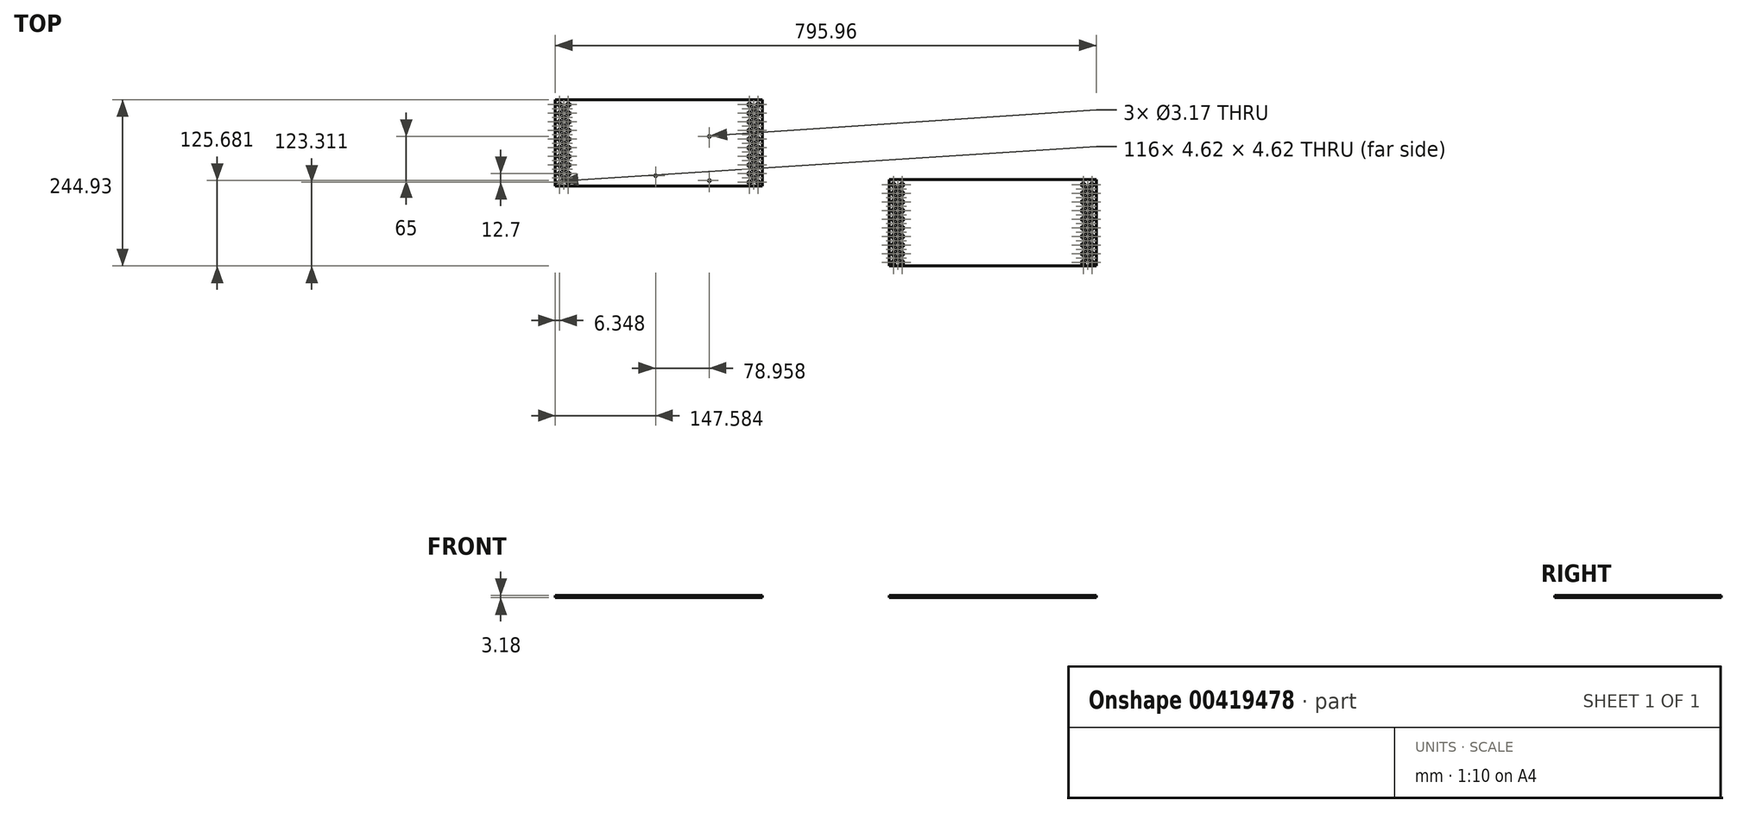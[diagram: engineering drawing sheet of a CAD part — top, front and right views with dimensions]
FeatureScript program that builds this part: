
annotation { "Feature Type Name" : "Feature", "Feature Type Description" : "" }
export const myFeature = defineFeature(function(context is Context, id is Id, definition is map)
    precondition{}
    {
        {
            var Q0;
            Q0=qCreatedBy(makeId("Top.planeOp"),FACE);
            var sketch = newSketch(context, id + "F0", { "sketchPlane" : qUnion([Q0])});
            skLineSegment(sketch, "E0", {"start": v(0, 0) * mm, "end": v(0, 127) * mm});
            skLineSegment(sketch, "E1", {"start": v(0, 127) * mm, "end": v(304.8, 127) * mm});
            skLineSegment(sketch, "E2", {"start": v(304.8, 127) * mm, "end": v(304.8, 0) * mm});
            skLineSegment(sketch, "E3", {"start": v(304.8, 0) * mm, "end": v(0, 0) * mm});
            skLineSegment(sketch, "E4", {"start": v(304.8, 0) * mm, "end": v(304.8, 127) * mm});
            skLineSegment(sketch, "E5", {"start": v(300.76, 3.07) * mm, "end": v(300.76, 7.7) * mm});
            skLineSegment(sketch, "E6.top", {"start": v(296.14, 3.07) * mm, "end": v(296.14, 7.7) * mm});
            skLineSegment(sketch, "E6.left", {"start": v(300.76, 3.07) * mm, "end": v(296.14, 3.07) * mm});
            skLineSegment(sketch, "E6.right", {"start": v(300.76, 7.7) * mm, "end": v(296.14, 7.7) * mm});
            skLineSegment(sketch, "E7", {"start": v(298.45, 7.7) * mm, "end": v(296.14, 7.7) * mm});
            skLineSegment(sketch, "E8", {"start": v(300.76, 5.38) * mm, "end": v(300.76, 7.7) * mm});
            skLineSegment(sketch, "E9.bottom", {"start": v(294.41, 9.42) * mm, "end": v(294.41, 14.05) * mm});
            skLineSegment(sketch, "E9.top", {"start": v(289.79, 9.42) * mm, "end": v(289.79, 14.05) * mm});
            skLineSegment(sketch, "E9.left", {"start": v(294.41, 9.42) * mm, "end": v(289.79, 9.42) * mm});
            skLineSegment(sketch, "E9.right", {"start": v(294.41, 14.05) * mm, "end": v(289.79, 14.05) * mm});
            skLineSegment(sketch, "E10.trimOffspring", {"start": v(300.76, 15.77) * mm, "end": v(300.76, 20.4) * mm});
            skLineSegment(sketch, "E11.1.0.0", {"start": v(289.79, 22.12) * mm, "end": v(289.79, 26.75) * mm});
            skLineSegment(sketch, "E11.1.0.1", {"start": v(294.41, 22.12) * mm, "end": v(294.41, 26.75) * mm});
            skLineSegment(sketch, "E11.1.0.2", {"start": v(294.41, 22.12) * mm, "end": v(289.79, 22.12) * mm});
            skLineSegment(sketch, "E11.1.0.3", {"start": v(294.41, 26.75) * mm, "end": v(289.79, 26.75) * mm});
            skLineSegment(sketch, "E11.1.0.4", {"start": v(300.76, 20.4) * mm, "end": v(296.14, 20.4) * mm});
            skLineSegment(sketch, "E11.1.0.5", {"start": v(296.14, 15.77) * mm, "end": v(296.14, 20.4) * mm});
            skLineSegment(sketch, "E11.1.0.6", {"start": v(300.76, 15.77) * mm, "end": v(296.14, 15.77) * mm});
            skLineSegment(sketch, "E11.2.0.0", {"start": v(289.79, 34.82) * mm, "end": v(289.79, 39.45) * mm});
            skLineSegment(sketch, "E11.2.0.1", {"start": v(294.41, 34.82) * mm, "end": v(294.41, 39.45) * mm});
            skLineSegment(sketch, "E11.2.0.2", {"start": v(294.41, 34.82) * mm, "end": v(289.79, 34.82) * mm});
            skLineSegment(sketch, "E11.2.0.3", {"start": v(294.41, 39.45) * mm, "end": v(289.79, 39.45) * mm});
            skLineSegment(sketch, "E11.2.0.4", {"start": v(300.76, 33.1) * mm, "end": v(296.14, 33.1) * mm});
            skLineSegment(sketch, "E11.2.0.5", {"start": v(296.14, 28.47) * mm, "end": v(296.14, 33.1) * mm});
            skLineSegment(sketch, "E11.2.0.6", {"start": v(300.76, 28.47) * mm, "end": v(296.14, 28.47) * mm});
            skLineSegment(sketch, "E11.2.0.7", {"start": v(300.76, 28.47) * mm, "end": v(300.76, 33.1) * mm});
            skLineSegment(sketch, "E11.3.0.0", {"start": v(289.79, 47.52) * mm, "end": v(289.79, 52.15) * mm});
            skLineSegment(sketch, "E11.3.0.1", {"start": v(294.41, 47.52) * mm, "end": v(294.41, 52.15) * mm});
            skLineSegment(sketch, "E11.3.0.2", {"start": v(294.41, 47.52) * mm, "end": v(289.79, 47.52) * mm});
            skLineSegment(sketch, "E11.3.0.3", {"start": v(294.41, 52.15) * mm, "end": v(289.79, 52.15) * mm});
            skLineSegment(sketch, "E11.3.0.4", {"start": v(300.76, 45.8) * mm, "end": v(296.14, 45.8) * mm});
            skLineSegment(sketch, "E11.3.0.5", {"start": v(296.14, 41.17) * mm, "end": v(296.14, 45.8) * mm});
            skLineSegment(sketch, "E11.3.0.6", {"start": v(300.76, 41.17) * mm, "end": v(296.14, 41.17) * mm});
            skLineSegment(sketch, "E11.3.0.7", {"start": v(300.76, 41.17) * mm, "end": v(300.76, 45.8) * mm});
            skLineSegment(sketch, "E11.4.0.0", {"start": v(289.79, 60.22) * mm, "end": v(289.79, 64.85) * mm});
            skLineSegment(sketch, "E11.4.0.1", {"start": v(294.41, 60.22) * mm, "end": v(294.41, 64.85) * mm});
            skLineSegment(sketch, "E11.4.0.2", {"start": v(294.41, 60.22) * mm, "end": v(289.79, 60.22) * mm});
            skLineSegment(sketch, "E11.4.0.3", {"start": v(294.41, 64.85) * mm, "end": v(289.79, 64.85) * mm});
            skLineSegment(sketch, "E11.4.0.4", {"start": v(300.76, 58.5) * mm, "end": v(296.14, 58.5) * mm});
            skLineSegment(sketch, "E11.4.0.5", {"start": v(296.14, 53.87) * mm, "end": v(296.14, 58.5) * mm});
            skLineSegment(sketch, "E11.4.0.6", {"start": v(300.76, 53.87) * mm, "end": v(296.14, 53.87) * mm});
            skLineSegment(sketch, "E11.4.0.7", {"start": v(300.76, 53.87) * mm, "end": v(300.76, 58.5) * mm});
            skLineSegment(sketch, "E11.5.0.0", {"start": v(289.79, 72.92) * mm, "end": v(289.79, 77.55) * mm});
            skLineSegment(sketch, "E11.5.0.1", {"start": v(294.41, 72.92) * mm, "end": v(294.41, 77.55) * mm});
            skLineSegment(sketch, "E11.5.0.2", {"start": v(294.41, 72.92) * mm, "end": v(289.79, 72.92) * mm});
            skLineSegment(sketch, "E11.5.0.3", {"start": v(294.41, 77.55) * mm, "end": v(289.79, 77.55) * mm});
            skLineSegment(sketch, "E11.5.0.4", {"start": v(300.76, 71.2) * mm, "end": v(296.14, 71.2) * mm});
            skLineSegment(sketch, "E11.5.0.5", {"start": v(296.14, 66.57) * mm, "end": v(296.14, 71.2) * mm});
            skLineSegment(sketch, "E11.5.0.6", {"start": v(300.76, 66.57) * mm, "end": v(296.14, 66.57) * mm});
            skLineSegment(sketch, "E11.5.0.7", {"start": v(300.76, 66.57) * mm, "end": v(300.76, 71.2) * mm});
            skLineSegment(sketch, "E11.6.0.0", {"start": v(289.79, 85.62) * mm, "end": v(289.79, 90.25) * mm});
            skLineSegment(sketch, "E11.6.0.1", {"start": v(294.41, 85.62) * mm, "end": v(294.41, 90.25) * mm});
            skLineSegment(sketch, "E11.6.0.2", {"start": v(294.41, 85.62) * mm, "end": v(289.79, 85.62) * mm});
            skLineSegment(sketch, "E11.6.0.3", {"start": v(294.41, 90.25) * mm, "end": v(289.79, 90.25) * mm});
            skLineSegment(sketch, "E11.6.0.4", {"start": v(300.76, 83.9) * mm, "end": v(296.14, 83.9) * mm});
            skLineSegment(sketch, "E11.6.0.5", {"start": v(296.14, 79.27) * mm, "end": v(296.14, 83.9) * mm});
            skLineSegment(sketch, "E11.6.0.6", {"start": v(300.76, 79.27) * mm, "end": v(296.14, 79.27) * mm});
            skLineSegment(sketch, "E11.6.0.7", {"start": v(300.76, 79.27) * mm, "end": v(300.76, 83.9) * mm});
            skLineSegment(sketch, "E11.7.0.0", {"start": v(289.79, 98.32) * mm, "end": v(289.79, 102.95) * mm});
            skLineSegment(sketch, "E11.7.0.1", {"start": v(294.41, 98.32) * mm, "end": v(294.41, 102.95) * mm});
            skLineSegment(sketch, "E11.7.0.2", {"start": v(294.41, 98.32) * mm, "end": v(289.79, 98.32) * mm});
            skLineSegment(sketch, "E11.7.0.3", {"start": v(294.41, 102.95) * mm, "end": v(289.79, 102.95) * mm});
            skLineSegment(sketch, "E11.7.0.4", {"start": v(300.76, 96.6) * mm, "end": v(296.14, 96.6) * mm});
            skLineSegment(sketch, "E11.7.0.5", {"start": v(296.14, 91.97) * mm, "end": v(296.14, 96.6) * mm});
            skLineSegment(sketch, "E11.7.0.6", {"start": v(300.76, 91.97) * mm, "end": v(296.14, 91.97) * mm});
            skLineSegment(sketch, "E11.7.0.7", {"start": v(300.76, 91.97) * mm, "end": v(300.76, 96.6) * mm});
            skLineSegment(sketch, "E11.8.0.0", {"start": v(289.79, 111.02) * mm, "end": v(289.79, 115.65) * mm});
            skLineSegment(sketch, "E11.8.0.1", {"start": v(294.41, 111.02) * mm, "end": v(294.41, 115.65) * mm});
            skLineSegment(sketch, "E11.8.0.2", {"start": v(294.41, 111.02) * mm, "end": v(289.79, 111.02) * mm});
            skLineSegment(sketch, "E11.8.0.3", {"start": v(294.41, 115.65) * mm, "end": v(289.79, 115.65) * mm});
            skLineSegment(sketch, "E11.8.0.4", {"start": v(300.76, 109.3) * mm, "end": v(296.14, 109.3) * mm});
            skLineSegment(sketch, "E11.8.0.5", {"start": v(296.14, 104.67) * mm, "end": v(296.14, 109.3) * mm});
            skLineSegment(sketch, "E11.8.0.6", {"start": v(300.76, 104.67) * mm, "end": v(296.14, 104.67) * mm});
            skLineSegment(sketch, "E11.8.0.7", {"start": v(300.76, 104.67) * mm, "end": v(300.76, 109.3) * mm});
            skLineSegment(sketch, "E11.9.0.4", {"start": v(300.76, 122) * mm, "end": v(296.14, 122) * mm});
            skLineSegment(sketch, "E11.9.0.5", {"start": v(296.14, 117.37) * mm, "end": v(296.14, 122) * mm});
            skLineSegment(sketch, "E11.9.0.6", {"start": v(300.76, 117.37) * mm, "end": v(296.14, 117.37) * mm});
            skLineSegment(sketch, "E11.9.0.7", {"start": v(300.76, 117.37) * mm, "end": v(300.76, 122) * mm});
            skLineSegment(sketch, "E11.direction1", {"start": v(294.41, 9.42) * mm, "end": v(294.41, 22.12) * mm, "construction": true});
            skLineSegment(sketch, "E12.1.0.20", {"start": v(288.06, 20.4) * mm, "end": v(283.44, 20.4) * mm});
            skLineSegment(sketch, "E12.1.0.21", {"start": v(288.06, 122) * mm, "end": v(283.44, 122) * mm});
            skLineSegment(sketch, "E12.1.0.22", {"start": v(288.06, 96.6) * mm, "end": v(283.44, 96.6) * mm});
            skLineSegment(sketch, "E12.1.0.23", {"start": v(288.06, 71.2) * mm, "end": v(283.44, 71.2) * mm});
            skLineSegment(sketch, "E12.1.0.24", {"start": v(288.06, 45.8) * mm, "end": v(283.44, 45.8) * mm});
            skLineSegment(sketch, "E12.1.0.36", {"start": v(283.44, 15.79) * mm, "end": v(283.44, 20.4) * mm});
            skLineSegment(sketch, "E12.1.0.39", {"start": v(283.44, 117.39) * mm, "end": v(283.44, 122) * mm});
            skLineSegment(sketch, "E12.1.0.41", {"start": v(283.44, 91.99) * mm, "end": v(283.44, 96.6) * mm});
            skLineSegment(sketch, "E12.1.0.42", {"start": v(283.44, 66.59) * mm, "end": v(283.44, 71.2) * mm});
            skLineSegment(sketch, "E12.1.0.43", {"start": v(283.44, 41.19) * mm, "end": v(283.44, 45.8) * mm});
            skLineSegment(sketch, "E12.1.0.49", {"start": v(288.06, 66.59) * mm, "end": v(283.44, 66.59) * mm});
            skLineSegment(sketch, "E12.1.0.50", {"start": v(288.06, 41.19) * mm, "end": v(283.44, 41.19) * mm});
            skLineSegment(sketch, "E12.1.0.51", {"start": v(288.06, 15.79) * mm, "end": v(283.44, 15.79) * mm});
            skLineSegment(sketch, "E12.1.0.54", {"start": v(288.06, 117.39) * mm, "end": v(283.44, 117.39) * mm});
            skLineSegment(sketch, "E12.1.0.55", {"start": v(288.06, 91.99) * mm, "end": v(283.44, 91.99) * mm});
            skLineSegment(sketch, "E12.1.0.59", {"start": v(288.06, 66.59) * mm, "end": v(288.06, 71.2) * mm});
            skLineSegment(sketch, "E12.1.0.96", {"start": v(288.06, 109.3) * mm, "end": v(283.44, 109.3) * mm});
            skLineSegment(sketch, "E12.1.0.97", {"start": v(288.06, 83.9) * mm, "end": v(283.44, 83.9) * mm});
            skLineSegment(sketch, "E12.1.0.98", {"start": v(288.06, 58.5) * mm, "end": v(283.44, 58.5) * mm});
            skLineSegment(sketch, "E12.1.0.99", {"start": v(288.06, 33.1) * mm, "end": v(283.44, 33.1) * mm});
            skLineSegment(sketch, "E12.1.0.116", {"start": v(283.44, 104.69) * mm, "end": v(283.44, 109.3) * mm});
            skLineSegment(sketch, "E12.1.0.117", {"start": v(283.44, 79.29) * mm, "end": v(283.44, 83.9) * mm});
            skLineSegment(sketch, "E12.1.0.118", {"start": v(283.44, 53.89) * mm, "end": v(283.44, 58.5) * mm});
            skLineSegment(sketch, "E12.1.0.119", {"start": v(283.44, 28.49) * mm, "end": v(283.44, 33.1) * mm});
            skLineSegment(sketch, "E12.1.0.125", {"start": v(288.06, 104.69) * mm, "end": v(283.44, 104.69) * mm});
            skLineSegment(sketch, "E12.1.0.126", {"start": v(288.06, 79.29) * mm, "end": v(283.44, 79.29) * mm});
            skLineSegment(sketch, "E12.1.0.127", {"start": v(288.06, 53.89) * mm, "end": v(283.44, 53.89) * mm});
            skLineSegment(sketch, "E12.1.0.128", {"start": v(288.06, 28.49) * mm, "end": v(283.44, 28.49) * mm});
            skLineSegment(sketch, "E12.1.0.137", {"start": v(283.44, 3.09) * mm, "end": v(283.44, 7.7) * mm});
            skLineSegment(sketch, "E12.1.0.138", {"start": v(288.06, 3.09) * mm, "end": v(283.44, 3.09) * mm});
            skLineSegment(sketch, "E12.1.0.154", {"start": v(288.06, 53.89) * mm, "end": v(288.06, 58.5) * mm});
            skLineSegment(sketch, "E12.1.0.155", {"start": v(288.06, 117.39) * mm, "end": v(288.06, 122) * mm});
            skLineSegment(sketch, "E12.1.0.156", {"start": v(288.06, 41.19) * mm, "end": v(288.06, 45.8) * mm});
            skLineSegment(sketch, "E12.1.0.157", {"start": v(285.75, 7.7) * mm, "end": v(283.44, 7.7) * mm});
            skLineSegment(sketch, "E12.1.0.159", {"start": v(288.06, 91.99) * mm, "end": v(288.06, 96.6) * mm});
            skLineSegment(sketch, "E12.1.0.160", {"start": v(288.06, 104.69) * mm, "end": v(288.06, 109.3) * mm});
            skLineSegment(sketch, "E12.1.0.161", {"start": v(288.06, 28.49) * mm, "end": v(288.06, 33.1) * mm});
            skLineSegment(sketch, "E12.1.0.162", {"start": v(288.06, 79.29) * mm, "end": v(288.06, 83.9) * mm});
            skLineSegment(sketch, "E12.1.0.163", {"start": v(288.06, 15.79) * mm, "end": v(288.06, 20.4) * mm});
            skLineSegment(sketch, "E12.1.0.164", {"start": v(288.06, 28.49) * mm, "end": v(288.06, 33.1) * mm});
            skLineSegment(sketch, "E12.1.0.166", {"start": v(288.06, 41.19) * mm, "end": v(288.06, 45.8) * mm});
            skLineSegment(sketch, "E12.1.0.167", {"start": v(288.06, 15.79) * mm, "end": v(288.06, 20.4) * mm});
            skLineSegment(sketch, "E12.1.0.168", {"start": v(288.06, 117.39) * mm, "end": v(288.06, 122) * mm});
            skLineSegment(sketch, "E12.1.0.169", {"start": v(288.06, 91.99) * mm, "end": v(288.06, 96.6) * mm});
            skLineSegment(sketch, "E12.1.0.170", {"start": v(288.06, 79.29) * mm, "end": v(288.06, 83.9) * mm});
            skLineSegment(sketch, "E12.1.0.171", {"start": v(288.06, 3.09) * mm, "end": v(288.06, 7.7) * mm});
            skLineSegment(sketch, "E12.1.0.172", {"start": v(288.06, 7.7) * mm, "end": v(283.44, 7.7) * mm});
            skLineSegment(sketch, "E12.1.0.173", {"start": v(288.06, 5.4) * mm, "end": v(288.06, 7.7) * mm});
            skLineSegment(sketch, "E12.1.0.174", {"start": v(288.06, 104.69) * mm, "end": v(288.06, 109.3) * mm});
            skLineSegment(sketch, "E12.1.0.175", {"start": v(288.06, 3.09) * mm, "end": v(288.06, 7.7) * mm});
            skLineSegment(sketch, "E13", {"start": v(279.4, 0) * mm, "end": v(304.8, 0) * mm});
            skLineSegment(sketch, "E14.MirrorCS", {"start": v(16.74, 3.09) * mm, "end": v(16.74, 7.7) * mm});
            skLineSegment(sketch, "E15.MirrorCS", {"start": v(4.04, 3.07) * mm, "end": v(4.04, 7.7) * mm});
            skLineSegment(sketch, "E16.MirrorCS", {"start": v(19.05, 7.7) * mm, "end": v(21.36, 7.7) * mm});
            skLineSegment(sketch, "E17.MirrorCS", {"start": v(16.74, 3.09) * mm, "end": v(21.36, 3.09) * mm});
            skLineSegment(sketch, "E18.MirrorCS", {"start": v(16.74, 7.7) * mm, "end": v(21.36, 7.7) * mm});
            skLineSegment(sketch, "E19.MirrorCS", {"start": v(16.74, 5.4) * mm, "end": v(16.74, 7.7) * mm});
            skLineSegment(sketch, "E20.MirrorCS", {"start": v(4.04, 7.7) * mm, "end": v(8.66, 7.7) * mm});
            skLineSegment(sketch, "E21.MirrorCS", {"start": v(8.66, 3.07) * mm, "end": v(8.66, 7.7) * mm});
            skLineSegment(sketch, "E22.MirrorCS", {"start": v(4.04, 3.07) * mm, "end": v(8.66, 3.07) * mm});
            skLineSegment(sketch, "E23.MirrorCS", {"start": v(6.35, 7.7) * mm, "end": v(8.66, 7.7) * mm});
            skLineSegment(sketch, "E24.MirrorCS", {"start": v(4.04, 5.38) * mm, "end": v(4.04, 7.7) * mm});
            skLineSegment(sketch, "E25.MirrorCS", {"start": v(16.74, 79.29) * mm, "end": v(16.74, 83.9) * mm});
            skLineSegment(sketch, "E26.MirrorCS", {"start": v(16.74, 15.79) * mm, "end": v(16.74, 20.4) * mm});
            skLineSegment(sketch, "E27.MirrorCS", {"start": v(16.74, 91.99) * mm, "end": v(16.74, 96.6) * mm});
            skLineSegment(sketch, "E28.MirrorCS", {"start": v(16.74, 41.19) * mm, "end": v(16.74, 45.8) * mm});
            skLineSegment(sketch, "E29.MirrorCS", {"start": v(16.74, 104.69) * mm, "end": v(16.74, 109.3) * mm});
            skLineSegment(sketch, "E30.MirrorCS", {"start": v(15.01, 9.42) * mm, "end": v(15.01, 14.05) * mm});
            skLineSegment(sketch, "E31.MirrorCS", {"start": v(10.39, 9.42) * mm, "end": v(15.01, 9.42) * mm});
            skLineSegment(sketch, "E32.MirrorCS", {"start": v(16.74, 28.49) * mm, "end": v(16.74, 33.1) * mm});
            skLineSegment(sketch, "E33.MirrorCS", {"start": v(15.01, 22.12) * mm, "end": v(15.01, 26.75) * mm});
            skLineSegment(sketch, "E34.MirrorCS", {"start": v(15.01, 72.92) * mm, "end": v(15.01, 77.55) * mm});
            skLineSegment(sketch, "E35.MirrorCS", {"start": v(15.01, 98.32) * mm, "end": v(15.01, 102.95) * mm});
            skLineSegment(sketch, "E36.MirrorCS", {"start": v(15.01, 47.52) * mm, "end": v(15.01, 52.15) * mm});
            skLineSegment(sketch, "E37.MirrorCS", {"start": v(4.04, 109.3) * mm, "end": v(8.66, 109.3) * mm});
            skLineSegment(sketch, "E38.MirrorCS", {"start": v(4.04, 83.9) * mm, "end": v(8.66, 83.9) * mm});
            skLineSegment(sketch, "E39.MirrorCS", {"start": v(4.04, 33.1) * mm, "end": v(8.66, 33.1) * mm});
            skLineSegment(sketch, "E40.MirrorCS", {"start": v(16.74, 83.9) * mm, "end": v(21.36, 83.9) * mm});
            skLineSegment(sketch, "E41.MirrorCS", {"start": v(10.39, 22.12) * mm, "end": v(10.39, 26.75) * mm});
            skLineSegment(sketch, "E42.MirrorCS", {"start": v(10.39, 98.32) * mm, "end": v(10.39, 102.95) * mm});
            skLineSegment(sketch, "E43.MirrorCS", {"start": v(10.39, 72.92) * mm, "end": v(10.39, 77.55) * mm});
            skLineSegment(sketch, "E44.MirrorCS", {"start": v(10.39, 47.52) * mm, "end": v(10.39, 52.15) * mm});
            skLineSegment(sketch, "E45.MirrorCS", {"start": v(10.39, 22.12) * mm, "end": v(15.01, 22.12) * mm});
            skLineSegment(sketch, "E46.MirrorCS", {"start": v(10.39, 98.32) * mm, "end": v(15.01, 98.32) * mm});
            skLineSegment(sketch, "E47.MirrorCS", {"start": v(10.39, 72.92) * mm, "end": v(15.01, 72.92) * mm});
            skLineSegment(sketch, "E48.MirrorCS", {"start": v(10.39, 47.52) * mm, "end": v(15.01, 47.52) * mm});
            skLineSegment(sketch, "E49.MirrorCS", {"start": v(8.66, 79.27) * mm, "end": v(8.66, 83.9) * mm});
            skLineSegment(sketch, "E50.MirrorCS", {"start": v(8.66, 28.47) * mm, "end": v(8.66, 33.1) * mm});
            skLineSegment(sketch, "E51.MirrorCS", {"start": v(8.66, 104.67) * mm, "end": v(8.66, 109.3) * mm});
            skLineSegment(sketch, "E52.MirrorCS", {"start": v(8.66, 53.87) * mm, "end": v(8.66, 58.5) * mm});
            skLineSegment(sketch, "E53.MirrorCS", {"start": v(10.39, 26.75) * mm, "end": v(15.01, 26.75) * mm});
            skLineSegment(sketch, "E54.MirrorCS", {"start": v(4.04, 117.37) * mm, "end": v(4.04, 122) * mm});
            skLineSegment(sketch, "E55.MirrorCS", {"start": v(10.39, 102.95) * mm, "end": v(15.01, 102.95) * mm});
            skLineSegment(sketch, "E56.MirrorCS", {"start": v(10.39, 77.55) * mm, "end": v(15.01, 77.55) * mm});
            skLineSegment(sketch, "E57.MirrorCS", {"start": v(16.74, 104.69) * mm, "end": v(21.36, 104.69) * mm});
            skLineSegment(sketch, "E58.MirrorCS", {"start": v(4.04, 20.4) * mm, "end": v(8.66, 20.4) * mm});
            skLineSegment(sketch, "E59.MirrorCS", {"start": v(10.39, 9.42) * mm, "end": v(10.39, 22.12) * mm, "construction": true});
            skLineSegment(sketch, "E60.MirrorCS", {"start": v(4.04, 96.6) * mm, "end": v(8.66, 96.6) * mm});
            skLineSegment(sketch, "E61.MirrorCS", {"start": v(4.04, 45.8) * mm, "end": v(8.66, 45.8) * mm});
            skLineSegment(sketch, "E62.MirrorCS", {"start": v(16.74, 79.29) * mm, "end": v(21.36, 79.29) * mm});
            skLineSegment(sketch, "E63.MirrorCS", {"start": v(8.66, 15.77) * mm, "end": v(8.66, 20.4) * mm});
            skLineSegment(sketch, "E64.MirrorCS", {"start": v(4.04, 41.17) * mm, "end": v(4.04, 45.8) * mm});
            skLineSegment(sketch, "E65.MirrorCS", {"start": v(8.66, 41.17) * mm, "end": v(8.66, 45.8) * mm});
            skLineSegment(sketch, "E66.MirrorCS", {"start": v(16.74, 117.39) * mm, "end": v(16.74, 122) * mm});
            skLineSegment(sketch, "E67.MirrorCS", {"start": v(16.74, 33.1) * mm, "end": v(21.36, 33.1) * mm});
            skLineSegment(sketch, "E68.MirrorCS", {"start": v(4.04, 28.47) * mm, "end": v(8.66, 28.47) * mm});
            skLineSegment(sketch, "E69.MirrorCS", {"start": v(4.04, 41.17) * mm, "end": v(8.66, 41.17) * mm});
            skLineSegment(sketch, "E70.MirrorCS", {"start": v(4.04, 15.77) * mm, "end": v(8.66, 15.77) * mm});
            skLineSegment(sketch, "E71.MirrorCS", {"start": v(16.74, 28.49) * mm, "end": v(21.36, 28.49) * mm});
            skLineSegment(sketch, "E72.MirrorCS", {"start": v(16.74, 41.19) * mm, "end": v(21.36, 41.19) * mm});
            skLineSegment(sketch, "E73.MirrorCS", {"start": v(21.36, 3.09) * mm, "end": v(21.36, 7.7) * mm});
            skLineSegment(sketch, "E74.MirrorCS", {"start": v(4.04, 91.97) * mm, "end": v(4.04, 96.6) * mm});
            skLineSegment(sketch, "E75.MirrorCS", {"start": v(15.01, 85.62) * mm, "end": v(15.01, 90.25) * mm});
            skLineSegment(sketch, "E76.MirrorCS", {"start": v(15.01, 60.22) * mm, "end": v(15.01, 64.85) * mm});
            skLineSegment(sketch, "E77.MirrorCS", {"start": v(15.01, 34.82) * mm, "end": v(15.01, 39.45) * mm});
            skLineSegment(sketch, "E78.MirrorCS", {"start": v(15.01, 111.02) * mm, "end": v(15.01, 115.65) * mm});
            skLineSegment(sketch, "E79.MirrorCS", {"start": v(10.39, 85.62) * mm, "end": v(10.39, 90.25) * mm});
            skLineSegment(sketch, "E80.MirrorCS", {"start": v(10.39, 60.22) * mm, "end": v(10.39, 64.85) * mm});
            skLineSegment(sketch, "E81.MirrorCS", {"start": v(10.39, 34.82) * mm, "end": v(10.39, 39.45) * mm});
            skLineSegment(sketch, "E82.MirrorCS", {"start": v(16.74, 91.99) * mm, "end": v(21.36, 91.99) * mm});
            skLineSegment(sketch, "E83.MirrorCS", {"start": v(10.39, 111.02) * mm, "end": v(10.39, 115.65) * mm});
            skLineSegment(sketch, "E84.MirrorCS", {"start": v(10.39, 85.62) * mm, "end": v(15.01, 85.62) * mm});
            skLineSegment(sketch, "E85.MirrorCS", {"start": v(10.39, 60.22) * mm, "end": v(15.01, 60.22) * mm});
            skLineSegment(sketch, "E86.MirrorCS", {"start": v(10.39, 111.02) * mm, "end": v(15.01, 111.02) * mm});
            skLineSegment(sketch, "E87.MirrorCS", {"start": v(10.39, 90.25) * mm, "end": v(15.01, 90.25) * mm});
            skLineSegment(sketch, "E88.MirrorCS", {"start": v(10.39, 115.65) * mm, "end": v(15.01, 115.65) * mm});
            skLineSegment(sketch, "E89.MirrorCS", {"start": v(10.39, 14.05) * mm, "end": v(15.01, 14.05) * mm});
            skLineSegment(sketch, "E90.MirrorCS", {"start": v(10.39, 9.42) * mm, "end": v(10.39, 14.05) * mm});
            skLineSegment(sketch, "E91.MirrorCS", {"start": v(16.74, 45.8) * mm, "end": v(21.36, 45.8) * mm});
            skLineSegment(sketch, "E92.MirrorCS", {"start": v(4.04, 15.77) * mm, "end": v(4.04, 20.4) * mm});
            skLineSegment(sketch, "E93.MirrorCS", {"start": v(4.04, 28.47) * mm, "end": v(4.04, 33.1) * mm});
            skLineSegment(sketch, "E94.MirrorCS", {"start": v(4.04, 79.27) * mm, "end": v(4.04, 83.9) * mm});
            skLineSegment(sketch, "E95.MirrorCS", {"start": v(4.04, 104.67) * mm, "end": v(4.04, 109.3) * mm});
            skLineSegment(sketch, "E96.MirrorCS", {"start": v(4.04, 122) * mm, "end": v(8.66, 122) * mm});
            skLineSegment(sketch, "E97.MirrorCS", {"start": v(4.04, 58.5) * mm, "end": v(8.66, 58.5) * mm});
            skLineSegment(sketch, "E98.MirrorCS", {"start": v(16.74, 122) * mm, "end": v(21.36, 122) * mm});
            skLineSegment(sketch, "E99.MirrorCS", {"start": v(4.04, 117.37) * mm, "end": v(8.66, 117.37) * mm});
            skLineSegment(sketch, "E100.MirrorCS", {"start": v(16.74, 96.6) * mm, "end": v(21.36, 96.6) * mm});
            skLineSegment(sketch, "E101.MirrorCS", {"start": v(16.74, 58.5) * mm, "end": v(21.36, 58.5) * mm});
            skLineSegment(sketch, "E102.MirrorCS", {"start": v(10.39, 52.15) * mm, "end": v(15.01, 52.15) * mm});
            skLineSegment(sketch, "E103.MirrorCS", {"start": v(4.04, 71.2) * mm, "end": v(8.66, 71.2) * mm});
            skLineSegment(sketch, "E104.MirrorCS", {"start": v(4.04, 104.67) * mm, "end": v(8.66, 104.67) * mm});
            skLineSegment(sketch, "E105.MirrorCS", {"start": v(8.66, 66.57) * mm, "end": v(8.66, 71.2) * mm});
            skLineSegment(sketch, "E106.MirrorCS", {"start": v(4.04, 53.87) * mm, "end": v(8.66, 53.87) * mm});
            skLineSegment(sketch, "E107.MirrorCS", {"start": v(4.04, 79.27) * mm, "end": v(8.66, 79.27) * mm});
            skLineSegment(sketch, "E108.MirrorCS", {"start": v(16.74, 71.2) * mm, "end": v(21.36, 71.2) * mm});
            skLineSegment(sketch, "E109.MirrorCS", {"start": v(16.74, 15.79) * mm, "end": v(21.36, 15.79) * mm});
            skLineSegment(sketch, "E110.MirrorCS", {"start": v(16.74, 117.39) * mm, "end": v(21.36, 117.39) * mm});
            skLineSegment(sketch, "E111.MirrorCS", {"start": v(16.74, 53.89) * mm, "end": v(16.74, 58.5) * mm});
            skLineSegment(sketch, "E112.MirrorCS", {"start": v(10.39, 34.82) * mm, "end": v(15.01, 34.82) * mm});
            skLineSegment(sketch, "E113.MirrorCS", {"start": v(16.74, 66.59) * mm, "end": v(16.74, 71.2) * mm});
            skLineSegment(sketch, "E114.MirrorCS", {"start": v(10.39, 64.85) * mm, "end": v(15.01, 64.85) * mm});
            skLineSegment(sketch, "E115.MirrorCS", {"start": v(10.39, 39.45) * mm, "end": v(15.01, 39.45) * mm});
            skLineSegment(sketch, "E116.MirrorCS", {"start": v(16.74, 109.3) * mm, "end": v(21.36, 109.3) * mm});
            skLineSegment(sketch, "E117.MirrorCS", {"start": v(16.74, 20.4) * mm, "end": v(21.36, 20.4) * mm});
            skLineSegment(sketch, "E118.MirrorCS", {"start": v(21.36, 79.29) * mm, "end": v(21.36, 83.9) * mm});
            skLineSegment(sketch, "E119.MirrorCS", {"start": v(21.36, 15.79) * mm, "end": v(21.36, 20.4) * mm});
            skLineSegment(sketch, "E120.MirrorCS", {"start": v(8.66, 117.37) * mm, "end": v(8.66, 122) * mm});
            skLineSegment(sketch, "E121.MirrorCS", {"start": v(21.36, 28.49) * mm, "end": v(21.36, 33.1) * mm});
            skLineSegment(sketch, "E122.MirrorCS", {"start": v(21.36, 91.99) * mm, "end": v(21.36, 96.6) * mm});
            skLineSegment(sketch, "E123.MirrorCS", {"start": v(21.36, 66.59) * mm, "end": v(21.36, 71.2) * mm});
            skLineSegment(sketch, "E124.MirrorCS", {"start": v(21.36, 41.19) * mm, "end": v(21.36, 45.8) * mm});
            skLineSegment(sketch, "E125.MirrorCS", {"start": v(16.74, 53.89) * mm, "end": v(21.36, 53.89) * mm});
            skLineSegment(sketch, "E126.MirrorCS", {"start": v(16.74, 66.59) * mm, "end": v(21.36, 66.59) * mm});
            skLineSegment(sketch, "E127.MirrorCS", {"start": v(4.04, 66.57) * mm, "end": v(8.66, 66.57) * mm});
            skLineSegment(sketch, "E128.MirrorCS", {"start": v(4.04, 66.57) * mm, "end": v(4.04, 71.2) * mm});
            skLineSegment(sketch, "E129.MirrorCS", {"start": v(21.36, 104.69) * mm, "end": v(21.36, 109.3) * mm});
            skLineSegment(sketch, "E130.MirrorCS", {"start": v(4.04, 53.87) * mm, "end": v(4.04, 58.5) * mm});
            skLineSegment(sketch, "E131.MirrorCS", {"start": v(21.36, 117.39) * mm, "end": v(21.36, 122) * mm});
            skLineSegment(sketch, "E132.MirrorCS", {"start": v(21.36, 53.89) * mm, "end": v(21.36, 58.5) * mm});
            skLineSegment(sketch, "E133", {"start": v(8.66, 96.6) * mm, "end": v(8.66, 91.99) * mm});
            skLineSegment(sketch, "E134", {"start": v(8.66, 91.99) * mm, "end": v(4.04, 91.97) * mm});
            skSolve(sketch);
        }
        {
            var Q0;
            Q0=makeQuery(id+"F0.imprint","IMPRINT",FACE,{"disambiguationData":[TD([[makeQuery(id+"F0.imprint","IMPRINT",EDGE,{"derivedFrom":sQuery(id+"F0.wireOp",EDGE,"E0")}),-1.0]])]});
            extrude(context, id + "F1", {"entities" : qUnion([Q0]), "depth" : 3.17 * mm});
        }
        {
            var Q0;
            Q0=qCreatedBy(makeId("Top.planeOp"),FACE);
            var sketch = newSketch(context, id + "F2", { "sketchPlane" : qUnion([Q0])});
            skLineSegment(sketch, "E135", {"start": v(-491.16, 117.93) * mm, "end": v(-491.16, 244.93) * mm});
            skLineSegment(sketch, "E136", {"start": v(-491.16, 244.93) * mm, "end": v(-186.36, 244.93) * mm});
            skLineSegment(sketch, "E137", {"start": v(-186.36, 244.93) * mm, "end": v(-186.36, 117.93) * mm});
            skLineSegment(sketch, "E138", {"start": v(-186.36, 117.93) * mm, "end": v(-491.16, 117.93) * mm});
            skLineSegment(sketch, "E139", {"start": v(-186.36, 117.93) * mm, "end": v(-186.36, 244.93) * mm});
            skLineSegment(sketch, "E140", {"start": v(-190.4, 121) * mm, "end": v(-190.4, 125.62) * mm});
            skLineSegment(sketch, "E141.top", {"start": v(-195.02, 121) * mm, "end": v(-195.02, 125.62) * mm});
            skLineSegment(sketch, "E141.left", {"start": v(-190.4, 121) * mm, "end": v(-195.02, 121) * mm});
            skLineSegment(sketch, "E141.right", {"start": v(-190.4, 125.62) * mm, "end": v(-195.02, 125.62) * mm});
            skLineSegment(sketch, "E142", {"start": v(-192.71, 125.62) * mm, "end": v(-195.02, 125.62) * mm});
            skLineSegment(sketch, "E143", {"start": v(-190.4, 123.31) * mm, "end": v(-190.4, 125.62) * mm});
            skLineSegment(sketch, "E144.bottom", {"start": v(-196.75, 127.35) * mm, "end": v(-196.75, 131.97) * mm});
            skLineSegment(sketch, "E144.top", {"start": v(-201.37, 127.35) * mm, "end": v(-201.37, 131.97) * mm});
            skLineSegment(sketch, "E144.left", {"start": v(-196.75, 127.35) * mm, "end": v(-201.37, 127.35) * mm});
            skLineSegment(sketch, "E144.right", {"start": v(-196.75, 131.97) * mm, "end": v(-201.37, 131.97) * mm});
            skLineSegment(sketch, "E145.trimOffspring", {"start": v(-190.4, 133.7) * mm, "end": v(-190.4, 138.32) * mm});
            skLineSegment(sketch, "E146.1.0.0", {"start": v(-201.37, 140.05) * mm, "end": v(-201.37, 144.67) * mm});
            skLineSegment(sketch, "E146.1.0.1", {"start": v(-196.75, 140.05) * mm, "end": v(-196.75, 144.67) * mm});
            skLineSegment(sketch, "E146.1.0.2", {"start": v(-196.75, 140.05) * mm, "end": v(-201.37, 140.05) * mm});
            skLineSegment(sketch, "E146.1.0.3", {"start": v(-196.75, 144.67) * mm, "end": v(-201.37, 144.67) * mm});
            skLineSegment(sketch, "E146.1.0.4", {"start": v(-190.4, 138.32) * mm, "end": v(-195.02, 138.32) * mm});
            skLineSegment(sketch, "E146.1.0.5", {"start": v(-195.02, 133.7) * mm, "end": v(-195.02, 138.32) * mm});
            skLineSegment(sketch, "E146.1.0.6", {"start": v(-190.4, 133.7) * mm, "end": v(-195.02, 133.7) * mm});
            skLineSegment(sketch, "E146.2.0.0", {"start": v(-201.37, 152.75) * mm, "end": v(-201.37, 157.37) * mm});
            skLineSegment(sketch, "E146.2.0.1", {"start": v(-196.75, 152.75) * mm, "end": v(-196.75, 157.37) * mm});
            skLineSegment(sketch, "E146.2.0.2", {"start": v(-196.75, 152.75) * mm, "end": v(-201.37, 152.75) * mm});
            skLineSegment(sketch, "E146.2.0.3", {"start": v(-196.75, 157.37) * mm, "end": v(-201.37, 157.37) * mm});
            skLineSegment(sketch, "E146.2.0.4", {"start": v(-190.4, 151.02) * mm, "end": v(-195.02, 151.02) * mm});
            skLineSegment(sketch, "E146.2.0.5", {"start": v(-195.02, 146.4) * mm, "end": v(-195.02, 151.02) * mm});
            skLineSegment(sketch, "E146.2.0.6", {"start": v(-190.4, 146.4) * mm, "end": v(-195.02, 146.4) * mm});
            skLineSegment(sketch, "E146.2.0.7", {"start": v(-190.4, 146.4) * mm, "end": v(-190.4, 151.02) * mm});
            skLineSegment(sketch, "E146.3.0.0", {"start": v(-201.37, 165.45) * mm, "end": v(-201.37, 170.07) * mm});
            skLineSegment(sketch, "E146.3.0.1", {"start": v(-196.75, 165.45) * mm, "end": v(-196.75, 170.07) * mm});
            skLineSegment(sketch, "E146.3.0.2", {"start": v(-196.75, 165.45) * mm, "end": v(-201.37, 165.45) * mm});
            skLineSegment(sketch, "E146.3.0.3", {"start": v(-196.75, 170.07) * mm, "end": v(-201.37, 170.07) * mm});
            skLineSegment(sketch, "E146.3.0.4", {"start": v(-190.4, 163.72) * mm, "end": v(-195.02, 163.72) * mm});
            skLineSegment(sketch, "E146.3.0.5", {"start": v(-195.02, 159.1) * mm, "end": v(-195.02, 163.72) * mm});
            skLineSegment(sketch, "E146.3.0.6", {"start": v(-190.4, 159.1) * mm, "end": v(-195.02, 159.1) * mm});
            skLineSegment(sketch, "E146.3.0.7", {"start": v(-190.4, 159.1) * mm, "end": v(-190.4, 163.72) * mm});
            skLineSegment(sketch, "E146.4.0.0", {"start": v(-201.37, 178.15) * mm, "end": v(-201.37, 182.77) * mm});
            skLineSegment(sketch, "E146.4.0.1", {"start": v(-196.75, 178.15) * mm, "end": v(-196.75, 182.77) * mm});
            skLineSegment(sketch, "E146.4.0.2", {"start": v(-196.75, 178.15) * mm, "end": v(-201.37, 178.15) * mm});
            skLineSegment(sketch, "E146.4.0.3", {"start": v(-196.75, 182.77) * mm, "end": v(-201.37, 182.77) * mm});
            skLineSegment(sketch, "E146.4.0.4", {"start": v(-190.4, 176.42) * mm, "end": v(-195.02, 176.42) * mm});
            skLineSegment(sketch, "E146.4.0.5", {"start": v(-195.02, 171.8) * mm, "end": v(-195.02, 176.42) * mm});
            skLineSegment(sketch, "E146.4.0.6", {"start": v(-190.4, 171.8) * mm, "end": v(-195.02, 171.8) * mm});
            skLineSegment(sketch, "E146.4.0.7", {"start": v(-190.4, 171.8) * mm, "end": v(-190.4, 176.42) * mm});
            skLineSegment(sketch, "E146.5.0.0", {"start": v(-201.37, 190.85) * mm, "end": v(-201.37, 195.47) * mm});
            skLineSegment(sketch, "E146.5.0.1", {"start": v(-196.75, 190.85) * mm, "end": v(-196.75, 195.47) * mm});
            skLineSegment(sketch, "E146.5.0.2", {"start": v(-196.75, 190.85) * mm, "end": v(-201.37, 190.85) * mm});
            skLineSegment(sketch, "E146.5.0.3", {"start": v(-196.75, 195.47) * mm, "end": v(-201.37, 195.47) * mm});
            skLineSegment(sketch, "E146.5.0.4", {"start": v(-190.4, 189.12) * mm, "end": v(-195.02, 189.12) * mm});
            skLineSegment(sketch, "E146.5.0.5", {"start": v(-195.02, 184.5) * mm, "end": v(-195.02, 189.12) * mm});
            skLineSegment(sketch, "E146.5.0.6", {"start": v(-190.4, 184.5) * mm, "end": v(-195.02, 184.5) * mm});
            skLineSegment(sketch, "E146.5.0.7", {"start": v(-190.4, 184.5) * mm, "end": v(-190.4, 189.12) * mm});
            skLineSegment(sketch, "E146.6.0.0", {"start": v(-201.37, 203.55) * mm, "end": v(-201.37, 208.17) * mm});
            skLineSegment(sketch, "E146.6.0.1", {"start": v(-196.75, 203.55) * mm, "end": v(-196.75, 208.17) * mm});
            skLineSegment(sketch, "E146.6.0.2", {"start": v(-196.75, 203.55) * mm, "end": v(-201.37, 203.55) * mm});
            skLineSegment(sketch, "E146.6.0.3", {"start": v(-196.75, 208.17) * mm, "end": v(-201.37, 208.17) * mm});
            skLineSegment(sketch, "E146.6.0.4", {"start": v(-190.4, 201.82) * mm, "end": v(-195.02, 201.82) * mm});
            skLineSegment(sketch, "E146.6.0.5", {"start": v(-195.02, 197.2) * mm, "end": v(-195.02, 201.82) * mm});
            skLineSegment(sketch, "E146.6.0.6", {"start": v(-190.4, 197.2) * mm, "end": v(-195.02, 197.2) * mm});
            skLineSegment(sketch, "E146.6.0.7", {"start": v(-190.4, 197.2) * mm, "end": v(-190.4, 201.82) * mm});
            skLineSegment(sketch, "E146.7.0.0", {"start": v(-201.37, 216.25) * mm, "end": v(-201.37, 220.87) * mm});
            skLineSegment(sketch, "E146.7.0.1", {"start": v(-196.75, 216.25) * mm, "end": v(-196.75, 220.87) * mm});
            skLineSegment(sketch, "E146.7.0.2", {"start": v(-196.75, 216.25) * mm, "end": v(-201.37, 216.25) * mm});
            skLineSegment(sketch, "E146.7.0.3", {"start": v(-196.75, 220.87) * mm, "end": v(-201.37, 220.87) * mm});
            skLineSegment(sketch, "E146.7.0.4", {"start": v(-190.4, 214.52) * mm, "end": v(-195.02, 214.52) * mm});
            skLineSegment(sketch, "E146.7.0.5", {"start": v(-195.02, 209.9) * mm, "end": v(-195.02, 214.52) * mm});
            skLineSegment(sketch, "E146.7.0.6", {"start": v(-190.4, 209.9) * mm, "end": v(-195.02, 209.9) * mm});
            skLineSegment(sketch, "E146.7.0.7", {"start": v(-190.4, 209.9) * mm, "end": v(-190.4, 214.52) * mm});
            skLineSegment(sketch, "E146.8.0.0", {"start": v(-201.37, 228.95) * mm, "end": v(-201.37, 233.57) * mm});
            skLineSegment(sketch, "E146.8.0.1", {"start": v(-196.75, 228.95) * mm, "end": v(-196.75, 233.57) * mm});
            skLineSegment(sketch, "E146.8.0.2", {"start": v(-196.75, 228.95) * mm, "end": v(-201.37, 228.95) * mm});
            skLineSegment(sketch, "E146.8.0.3", {"start": v(-196.75, 233.57) * mm, "end": v(-201.37, 233.57) * mm});
            skLineSegment(sketch, "E146.8.0.4", {"start": v(-190.4, 227.22) * mm, "end": v(-195.02, 227.22) * mm});
            skLineSegment(sketch, "E146.8.0.5", {"start": v(-195.02, 222.6) * mm, "end": v(-195.02, 227.22) * mm});
            skLineSegment(sketch, "E146.8.0.6", {"start": v(-190.4, 222.6) * mm, "end": v(-195.02, 222.6) * mm});
            skLineSegment(sketch, "E146.8.0.7", {"start": v(-190.4, 222.6) * mm, "end": v(-190.4, 227.22) * mm});
            skLineSegment(sketch, "E146.9.0.4", {"start": v(-190.4, 239.92) * mm, "end": v(-195.02, 239.92) * mm});
            skLineSegment(sketch, "E146.9.0.5", {"start": v(-195.02, 235.3) * mm, "end": v(-195.02, 239.92) * mm});
            skLineSegment(sketch, "E146.9.0.6", {"start": v(-190.4, 235.3) * mm, "end": v(-195.02, 235.3) * mm});
            skLineSegment(sketch, "E146.9.0.7", {"start": v(-190.4, 235.3) * mm, "end": v(-190.4, 239.92) * mm});
            skLineSegment(sketch, "E146.direction1", {"start": v(-196.75, 127.35) * mm, "end": v(-196.75, 140.05) * mm, "construction": true});
            skLineSegment(sketch, "E147.1.0.20", {"start": v(-203.1, 138.33) * mm, "end": v(-207.72, 138.33) * mm});
            skLineSegment(sketch, "E147.1.0.21", {"start": v(-203.1, 239.93) * mm, "end": v(-207.72, 239.93) * mm});
            skLineSegment(sketch, "E147.1.0.22", {"start": v(-203.1, 214.53) * mm, "end": v(-207.72, 214.53) * mm});
            skLineSegment(sketch, "E147.1.0.23", {"start": v(-203.1, 189.13) * mm, "end": v(-207.72, 189.13) * mm});
            skLineSegment(sketch, "E147.1.0.24", {"start": v(-203.1, 163.73) * mm, "end": v(-207.72, 163.73) * mm});
            skLineSegment(sketch, "E147.1.0.36", {"start": v(-207.72, 133.71) * mm, "end": v(-207.72, 138.33) * mm});
            skLineSegment(sketch, "E147.1.0.39", {"start": v(-207.72, 235.31) * mm, "end": v(-207.72, 239.93) * mm});
            skLineSegment(sketch, "E147.1.0.41", {"start": v(-207.72, 209.91) * mm, "end": v(-207.72, 214.53) * mm});
            skLineSegment(sketch, "E147.1.0.42", {"start": v(-207.72, 184.51) * mm, "end": v(-207.72, 189.13) * mm});
            skLineSegment(sketch, "E147.1.0.43", {"start": v(-207.72, 159.11) * mm, "end": v(-207.72, 163.73) * mm});
            skLineSegment(sketch, "E147.1.0.49", {"start": v(-203.1, 184.51) * mm, "end": v(-207.72, 184.51) * mm});
            skLineSegment(sketch, "E147.1.0.50", {"start": v(-203.1, 159.11) * mm, "end": v(-207.72, 159.11) * mm});
            skLineSegment(sketch, "E147.1.0.51", {"start": v(-203.1, 133.71) * mm, "end": v(-207.72, 133.71) * mm});
            skLineSegment(sketch, "E147.1.0.54", {"start": v(-203.1, 235.31) * mm, "end": v(-207.72, 235.31) * mm});
            skLineSegment(sketch, "E147.1.0.55", {"start": v(-203.1, 209.91) * mm, "end": v(-207.72, 209.91) * mm});
            skLineSegment(sketch, "E147.1.0.59", {"start": v(-203.1, 184.51) * mm, "end": v(-203.1, 189.13) * mm});
            skLineSegment(sketch, "E147.1.0.96", {"start": v(-203.1, 227.23) * mm, "end": v(-207.72, 227.23) * mm});
            skLineSegment(sketch, "E147.1.0.97", {"start": v(-203.1, 201.83) * mm, "end": v(-207.72, 201.83) * mm});
            skLineSegment(sketch, "E147.1.0.98", {"start": v(-203.1, 176.43) * mm, "end": v(-207.72, 176.43) * mm});
            skLineSegment(sketch, "E147.1.0.99", {"start": v(-203.1, 151.03) * mm, "end": v(-207.72, 151.03) * mm});
            skLineSegment(sketch, "E147.1.0.116", {"start": v(-207.72, 222.61) * mm, "end": v(-207.72, 227.23) * mm});
            skLineSegment(sketch, "E147.1.0.117", {"start": v(-207.72, 197.21) * mm, "end": v(-207.72, 201.83) * mm});
            skLineSegment(sketch, "E147.1.0.118", {"start": v(-207.72, 171.81) * mm, "end": v(-207.72, 176.43) * mm});
            skLineSegment(sketch, "E147.1.0.119", {"start": v(-207.72, 146.41) * mm, "end": v(-207.72, 151.03) * mm});
            skLineSegment(sketch, "E147.1.0.125", {"start": v(-203.1, 222.61) * mm, "end": v(-207.72, 222.61) * mm});
            skLineSegment(sketch, "E147.1.0.126", {"start": v(-203.1, 197.21) * mm, "end": v(-207.72, 197.21) * mm});
            skLineSegment(sketch, "E147.1.0.127", {"start": v(-203.1, 171.81) * mm, "end": v(-207.72, 171.81) * mm});
            skLineSegment(sketch, "E147.1.0.128", {"start": v(-203.1, 146.41) * mm, "end": v(-207.72, 146.41) * mm});
            skLineSegment(sketch, "E147.1.0.137", {"start": v(-207.72, 121.01) * mm, "end": v(-207.72, 125.63) * mm});
            skLineSegment(sketch, "E147.1.0.138", {"start": v(-203.1, 121.01) * mm, "end": v(-207.72, 121.01) * mm});
            skLineSegment(sketch, "E147.1.0.154", {"start": v(-203.1, 171.81) * mm, "end": v(-203.1, 176.43) * mm});
            skLineSegment(sketch, "E147.1.0.155", {"start": v(-203.1, 235.31) * mm, "end": v(-203.1, 239.93) * mm});
            skLineSegment(sketch, "E147.1.0.156", {"start": v(-203.1, 159.11) * mm, "end": v(-203.1, 163.73) * mm});
            skLineSegment(sketch, "E147.1.0.157", {"start": v(-205.41, 125.63) * mm, "end": v(-207.72, 125.63) * mm});
            skLineSegment(sketch, "E147.1.0.159", {"start": v(-203.1, 209.91) * mm, "end": v(-203.1, 214.53) * mm});
            skLineSegment(sketch, "E147.1.0.160", {"start": v(-203.1, 222.61) * mm, "end": v(-203.1, 227.23) * mm});
            skLineSegment(sketch, "E147.1.0.161", {"start": v(-203.1, 146.41) * mm, "end": v(-203.1, 151.03) * mm});
            skLineSegment(sketch, "E147.1.0.162", {"start": v(-203.1, 197.21) * mm, "end": v(-203.1, 201.83) * mm});
            skLineSegment(sketch, "E147.1.0.163", {"start": v(-203.1, 133.71) * mm, "end": v(-203.1, 138.33) * mm});
            skLineSegment(sketch, "E147.1.0.164", {"start": v(-203.1, 146.41) * mm, "end": v(-203.1, 151.03) * mm});
            skLineSegment(sketch, "E147.1.0.166", {"start": v(-203.1, 159.11) * mm, "end": v(-203.1, 163.73) * mm});
            skLineSegment(sketch, "E147.1.0.167", {"start": v(-203.1, 133.71) * mm, "end": v(-203.1, 138.33) * mm});
            skLineSegment(sketch, "E147.1.0.168", {"start": v(-203.1, 235.31) * mm, "end": v(-203.1, 239.93) * mm});
            skLineSegment(sketch, "E147.1.0.169", {"start": v(-203.1, 209.91) * mm, "end": v(-203.1, 214.53) * mm});
            skLineSegment(sketch, "E147.1.0.170", {"start": v(-203.1, 197.21) * mm, "end": v(-203.1, 201.83) * mm});
            skLineSegment(sketch, "E147.1.0.171", {"start": v(-203.1, 121.01) * mm, "end": v(-203.1, 125.63) * mm});
            skLineSegment(sketch, "E147.1.0.172", {"start": v(-203.1, 125.63) * mm, "end": v(-207.72, 125.63) * mm});
            skLineSegment(sketch, "E147.1.0.173", {"start": v(-203.1, 123.32) * mm, "end": v(-203.1, 125.63) * mm});
            skLineSegment(sketch, "E147.1.0.174", {"start": v(-203.1, 222.61) * mm, "end": v(-203.1, 227.23) * mm});
            skLineSegment(sketch, "E147.1.0.175", {"start": v(-203.1, 121.01) * mm, "end": v(-203.1, 125.63) * mm});
            skLineSegment(sketch, "E148", {"start": v(-211.76, 117.93) * mm, "end": v(-186.36, 117.93) * mm});
            skLineSegment(sketch, "E149.MirrorCS", {"start": v(-474.42, 121.01) * mm, "end": v(-474.42, 125.63) * mm});
            skLineSegment(sketch, "E150.MirrorCS", {"start": v(-487.12, 121) * mm, "end": v(-487.12, 125.62) * mm});
            skLineSegment(sketch, "E151.MirrorCS", {"start": v(-472.11, 125.63) * mm, "end": v(-469.8, 125.63) * mm});
            skLineSegment(sketch, "E152.MirrorCS", {"start": v(-474.42, 121.01) * mm, "end": v(-469.8, 121.01) * mm});
            skLineSegment(sketch, "E153.MirrorCS", {"start": v(-474.42, 125.63) * mm, "end": v(-469.8, 125.63) * mm});
            skLineSegment(sketch, "E154.MirrorCS", {"start": v(-474.42, 123.32) * mm, "end": v(-474.42, 125.63) * mm});
            skLineSegment(sketch, "E155.MirrorCS", {"start": v(-487.12, 125.62) * mm, "end": v(-482.5, 125.62) * mm});
            skLineSegment(sketch, "E156.MirrorCS", {"start": v(-482.5, 121) * mm, "end": v(-482.5, 125.62) * mm});
            skLineSegment(sketch, "E157.MirrorCS", {"start": v(-487.12, 121) * mm, "end": v(-482.5, 121) * mm});
            skLineSegment(sketch, "E158.MirrorCS", {"start": v(-484.81, 125.62) * mm, "end": v(-482.5, 125.62) * mm});
            skLineSegment(sketch, "E159.MirrorCS", {"start": v(-487.12, 123.31) * mm, "end": v(-487.12, 125.62) * mm});
            skLineSegment(sketch, "E160.MirrorCS", {"start": v(-474.42, 197.21) * mm, "end": v(-474.42, 201.83) * mm});
            skLineSegment(sketch, "E161.MirrorCS", {"start": v(-474.42, 133.71) * mm, "end": v(-474.42, 138.33) * mm});
            skLineSegment(sketch, "E162.MirrorCS", {"start": v(-474.42, 209.91) * mm, "end": v(-474.42, 214.53) * mm});
            skLineSegment(sketch, "E163.MirrorCS", {"start": v(-474.42, 159.11) * mm, "end": v(-474.42, 163.73) * mm});
            skLineSegment(sketch, "E164.MirrorCS", {"start": v(-474.42, 222.61) * mm, "end": v(-474.42, 227.23) * mm});
            skLineSegment(sketch, "E165.MirrorCS", {"start": v(-476.15, 127.35) * mm, "end": v(-476.15, 131.97) * mm});
            skLineSegment(sketch, "E166.MirrorCS", {"start": v(-480.77, 127.35) * mm, "end": v(-476.15, 127.35) * mm});
            skLineSegment(sketch, "E167.MirrorCS", {"start": v(-474.42, 146.41) * mm, "end": v(-474.42, 151.03) * mm});
            skLineSegment(sketch, "E168.MirrorCS", {"start": v(-476.15, 140.05) * mm, "end": v(-476.15, 144.67) * mm});
            skLineSegment(sketch, "E169.MirrorCS", {"start": v(-476.15, 190.85) * mm, "end": v(-476.15, 195.47) * mm});
            skLineSegment(sketch, "E170.MirrorCS", {"start": v(-476.15, 216.25) * mm, "end": v(-476.15, 220.87) * mm});
            skLineSegment(sketch, "E171.MirrorCS", {"start": v(-476.15, 165.45) * mm, "end": v(-476.15, 170.07) * mm});
            skLineSegment(sketch, "E172.MirrorCS", {"start": v(-487.12, 227.22) * mm, "end": v(-482.5, 227.22) * mm});
            skLineSegment(sketch, "E173.MirrorCS", {"start": v(-487.12, 201.82) * mm, "end": v(-482.5, 201.82) * mm});
            skLineSegment(sketch, "E174.MirrorCS", {"start": v(-487.12, 151.02) * mm, "end": v(-482.5, 151.02) * mm});
            skLineSegment(sketch, "E175.MirrorCS", {"start": v(-474.42, 201.83) * mm, "end": v(-469.8, 201.83) * mm});
            skLineSegment(sketch, "E176.MirrorCS", {"start": v(-480.77, 140.05) * mm, "end": v(-480.77, 144.67) * mm});
            skLineSegment(sketch, "E177.MirrorCS", {"start": v(-480.77, 216.25) * mm, "end": v(-480.77, 220.87) * mm});
            skLineSegment(sketch, "E178.MirrorCS", {"start": v(-480.77, 190.85) * mm, "end": v(-480.77, 195.47) * mm});
            skLineSegment(sketch, "E179.MirrorCS", {"start": v(-480.77, 165.45) * mm, "end": v(-480.77, 170.07) * mm});
            skLineSegment(sketch, "E180.MirrorCS", {"start": v(-480.77, 140.05) * mm, "end": v(-476.15, 140.05) * mm});
            skLineSegment(sketch, "E181.MirrorCS", {"start": v(-480.77, 216.25) * mm, "end": v(-476.15, 216.25) * mm});
            skLineSegment(sketch, "E182.MirrorCS", {"start": v(-480.77, 190.85) * mm, "end": v(-476.15, 190.85) * mm});
            skLineSegment(sketch, "E183.MirrorCS", {"start": v(-480.77, 165.45) * mm, "end": v(-476.15, 165.45) * mm});
            skLineSegment(sketch, "E184.MirrorCS", {"start": v(-482.5, 197.2) * mm, "end": v(-482.5, 201.82) * mm});
            skLineSegment(sketch, "E185.MirrorCS", {"start": v(-482.5, 146.4) * mm, "end": v(-482.5, 151.02) * mm});
            skLineSegment(sketch, "E186.MirrorCS", {"start": v(-482.5, 222.6) * mm, "end": v(-482.5, 227.22) * mm});
            skLineSegment(sketch, "E187.MirrorCS", {"start": v(-482.5, 171.8) * mm, "end": v(-482.5, 176.42) * mm});
            skLineSegment(sketch, "E188.MirrorCS", {"start": v(-480.77, 144.67) * mm, "end": v(-476.15, 144.67) * mm});
            skLineSegment(sketch, "E189.MirrorCS", {"start": v(-487.12, 235.3) * mm, "end": v(-487.12, 239.92) * mm});
            skLineSegment(sketch, "E190.MirrorCS", {"start": v(-480.77, 220.87) * mm, "end": v(-476.15, 220.87) * mm});
            skLineSegment(sketch, "E191.MirrorCS", {"start": v(-480.77, 195.47) * mm, "end": v(-476.15, 195.47) * mm});
            skLineSegment(sketch, "E192.MirrorCS", {"start": v(-474.42, 222.61) * mm, "end": v(-469.8, 222.61) * mm});
            skLineSegment(sketch, "E193.MirrorCS", {"start": v(-487.12, 138.32) * mm, "end": v(-482.5, 138.32) * mm});
            skLineSegment(sketch, "E194.MirrorCS", {"start": v(-480.77, 127.35) * mm, "end": v(-480.77, 140.05) * mm, "construction": true});
            skLineSegment(sketch, "E195.MirrorCS", {"start": v(-487.12, 214.52) * mm, "end": v(-482.5, 214.52) * mm});
            skLineSegment(sketch, "E196.MirrorCS", {"start": v(-487.12, 163.72) * mm, "end": v(-482.5, 163.72) * mm});
            skLineSegment(sketch, "E197.MirrorCS", {"start": v(-474.42, 197.21) * mm, "end": v(-469.8, 197.21) * mm});
            skLineSegment(sketch, "E198.MirrorCS", {"start": v(-482.5, 133.7) * mm, "end": v(-482.5, 138.32) * mm});
            skLineSegment(sketch, "E199.MirrorCS", {"start": v(-487.12, 159.1) * mm, "end": v(-487.12, 163.72) * mm});
            skLineSegment(sketch, "E200.MirrorCS", {"start": v(-482.5, 159.1) * mm, "end": v(-482.5, 163.72) * mm});
            skLineSegment(sketch, "E201.MirrorCS", {"start": v(-474.42, 235.31) * mm, "end": v(-474.42, 239.93) * mm});
            skLineSegment(sketch, "E202.MirrorCS", {"start": v(-474.42, 151.03) * mm, "end": v(-469.8, 151.03) * mm});
            skLineSegment(sketch, "E203.MirrorCS", {"start": v(-487.12, 146.4) * mm, "end": v(-482.5, 146.4) * mm});
            skLineSegment(sketch, "E204.MirrorCS", {"start": v(-487.12, 159.1) * mm, "end": v(-482.5, 159.1) * mm});
            skLineSegment(sketch, "E205.MirrorCS", {"start": v(-487.12, 133.7) * mm, "end": v(-482.5, 133.7) * mm});
            skLineSegment(sketch, "E206.MirrorCS", {"start": v(-474.42, 146.41) * mm, "end": v(-469.8, 146.41) * mm});
            skLineSegment(sketch, "E207.MirrorCS", {"start": v(-474.42, 159.11) * mm, "end": v(-469.8, 159.11) * mm});
            skLineSegment(sketch, "E208.MirrorCS", {"start": v(-469.8, 121.01) * mm, "end": v(-469.8, 125.63) * mm});
            skLineSegment(sketch, "E209.MirrorCS", {"start": v(-487.12, 209.9) * mm, "end": v(-487.12, 214.52) * mm});
            skLineSegment(sketch, "E210.MirrorCS", {"start": v(-476.15, 203.55) * mm, "end": v(-476.15, 208.17) * mm});
            skLineSegment(sketch, "E211.MirrorCS", {"start": v(-476.15, 178.15) * mm, "end": v(-476.15, 182.77) * mm});
            skLineSegment(sketch, "E212.MirrorCS", {"start": v(-476.15, 152.75) * mm, "end": v(-476.15, 157.37) * mm});
            skLineSegment(sketch, "E213.MirrorCS", {"start": v(-476.15, 228.95) * mm, "end": v(-476.15, 233.57) * mm});
            skLineSegment(sketch, "E214.MirrorCS", {"start": v(-480.77, 203.55) * mm, "end": v(-480.77, 208.17) * mm});
            skLineSegment(sketch, "E215.MirrorCS", {"start": v(-480.77, 178.15) * mm, "end": v(-480.77, 182.77) * mm});
            skLineSegment(sketch, "E216.MirrorCS", {"start": v(-480.77, 152.75) * mm, "end": v(-480.77, 157.37) * mm});
            skLineSegment(sketch, "E217.MirrorCS", {"start": v(-474.42, 209.91) * mm, "end": v(-469.8, 209.91) * mm});
            skLineSegment(sketch, "E218.MirrorCS", {"start": v(-480.77, 228.95) * mm, "end": v(-480.77, 233.57) * mm});
            skLineSegment(sketch, "E219.MirrorCS", {"start": v(-480.77, 203.55) * mm, "end": v(-476.15, 203.55) * mm});
            skLineSegment(sketch, "E220.MirrorCS", {"start": v(-480.77, 178.15) * mm, "end": v(-476.15, 178.15) * mm});
            skLineSegment(sketch, "E221.MirrorCS", {"start": v(-480.77, 228.95) * mm, "end": v(-476.15, 228.95) * mm});
            skLineSegment(sketch, "E222.MirrorCS", {"start": v(-480.77, 208.17) * mm, "end": v(-476.15, 208.17) * mm});
            skLineSegment(sketch, "E223.MirrorCS", {"start": v(-480.77, 233.57) * mm, "end": v(-476.15, 233.57) * mm});
            skLineSegment(sketch, "E224.MirrorCS", {"start": v(-480.77, 131.97) * mm, "end": v(-476.15, 131.97) * mm});
            skLineSegment(sketch, "E225.MirrorCS", {"start": v(-480.77, 127.35) * mm, "end": v(-480.77, 131.97) * mm});
            skLineSegment(sketch, "E226.MirrorCS", {"start": v(-474.42, 163.73) * mm, "end": v(-469.8, 163.73) * mm});
            skLineSegment(sketch, "E227.MirrorCS", {"start": v(-487.12, 133.7) * mm, "end": v(-487.12, 138.32) * mm});
            skLineSegment(sketch, "E228.MirrorCS", {"start": v(-487.12, 146.4) * mm, "end": v(-487.12, 151.02) * mm});
            skLineSegment(sketch, "E229.MirrorCS", {"start": v(-487.12, 197.2) * mm, "end": v(-487.12, 201.82) * mm});
            skLineSegment(sketch, "E230.MirrorCS", {"start": v(-487.12, 222.6) * mm, "end": v(-487.12, 227.22) * mm});
            skLineSegment(sketch, "E231.MirrorCS", {"start": v(-487.12, 239.92) * mm, "end": v(-482.5, 239.92) * mm});
            skLineSegment(sketch, "E232.MirrorCS", {"start": v(-487.12, 176.42) * mm, "end": v(-482.5, 176.42) * mm});
            skLineSegment(sketch, "E233.MirrorCS", {"start": v(-474.42, 239.93) * mm, "end": v(-469.8, 239.93) * mm});
            skLineSegment(sketch, "E234.MirrorCS", {"start": v(-487.12, 235.3) * mm, "end": v(-482.5, 235.3) * mm});
            skLineSegment(sketch, "E235.MirrorCS", {"start": v(-474.42, 214.53) * mm, "end": v(-469.8, 214.53) * mm});
            skLineSegment(sketch, "E236.MirrorCS", {"start": v(-474.42, 176.43) * mm, "end": v(-469.8, 176.43) * mm});
            skLineSegment(sketch, "E237.MirrorCS", {"start": v(-480.77, 170.07) * mm, "end": v(-476.15, 170.07) * mm});
            skLineSegment(sketch, "E238.MirrorCS", {"start": v(-487.12, 189.12) * mm, "end": v(-482.5, 189.12) * mm});
            skLineSegment(sketch, "E239.MirrorCS", {"start": v(-487.12, 222.6) * mm, "end": v(-482.5, 222.6) * mm});
            skLineSegment(sketch, "E240.MirrorCS", {"start": v(-482.5, 184.5) * mm, "end": v(-482.5, 189.12) * mm});
            skLineSegment(sketch, "E241.MirrorCS", {"start": v(-487.12, 171.8) * mm, "end": v(-482.5, 171.8) * mm});
            skLineSegment(sketch, "E242.MirrorCS", {"start": v(-487.12, 197.2) * mm, "end": v(-482.5, 197.2) * mm});
            skLineSegment(sketch, "E243.MirrorCS", {"start": v(-474.42, 189.13) * mm, "end": v(-469.8, 189.13) * mm});
            skLineSegment(sketch, "E244.MirrorCS", {"start": v(-474.42, 133.71) * mm, "end": v(-469.8, 133.71) * mm});
            skLineSegment(sketch, "E245.MirrorCS", {"start": v(-474.42, 235.31) * mm, "end": v(-469.8, 235.31) * mm});
            skLineSegment(sketch, "E246.MirrorCS", {"start": v(-474.42, 171.81) * mm, "end": v(-474.42, 176.43) * mm});
            skLineSegment(sketch, "E247.MirrorCS", {"start": v(-480.77, 152.75) * mm, "end": v(-476.15, 152.75) * mm});
            skLineSegment(sketch, "E248.MirrorCS", {"start": v(-474.42, 184.51) * mm, "end": v(-474.42, 189.13) * mm});
            skLineSegment(sketch, "E249.MirrorCS", {"start": v(-480.77, 182.77) * mm, "end": v(-476.15, 182.77) * mm});
            skLineSegment(sketch, "E250.MirrorCS", {"start": v(-480.77, 157.37) * mm, "end": v(-476.15, 157.37) * mm});
            skLineSegment(sketch, "E251.MirrorCS", {"start": v(-474.42, 227.23) * mm, "end": v(-469.8, 227.23) * mm});
            skLineSegment(sketch, "E252.MirrorCS", {"start": v(-474.42, 138.33) * mm, "end": v(-469.8, 138.33) * mm});
            skLineSegment(sketch, "E253.MirrorCS", {"start": v(-469.8, 197.21) * mm, "end": v(-469.8, 201.83) * mm});
            skLineSegment(sketch, "E254.MirrorCS", {"start": v(-469.8, 133.71) * mm, "end": v(-469.8, 138.33) * mm});
            skLineSegment(sketch, "E255.MirrorCS", {"start": v(-482.5, 235.3) * mm, "end": v(-482.5, 239.92) * mm});
            skLineSegment(sketch, "E256.MirrorCS", {"start": v(-469.8, 146.41) * mm, "end": v(-469.8, 151.03) * mm});
            skLineSegment(sketch, "E257.MirrorCS", {"start": v(-469.8, 209.91) * mm, "end": v(-469.8, 214.53) * mm});
            skLineSegment(sketch, "E258.MirrorCS", {"start": v(-469.8, 184.51) * mm, "end": v(-469.8, 189.13) * mm});
            skLineSegment(sketch, "E259.MirrorCS", {"start": v(-469.8, 159.11) * mm, "end": v(-469.8, 163.73) * mm});
            skLineSegment(sketch, "E260.MirrorCS", {"start": v(-474.42, 171.81) * mm, "end": v(-469.8, 171.81) * mm});
            skLineSegment(sketch, "E261.MirrorCS", {"start": v(-474.42, 184.51) * mm, "end": v(-469.8, 184.51) * mm});
            skLineSegment(sketch, "E262.MirrorCS", {"start": v(-487.12, 184.5) * mm, "end": v(-482.5, 184.5) * mm});
            skLineSegment(sketch, "E263.MirrorCS", {"start": v(-487.12, 184.5) * mm, "end": v(-487.12, 189.12) * mm});
            skLineSegment(sketch, "E264.MirrorCS", {"start": v(-469.8, 222.61) * mm, "end": v(-469.8, 227.23) * mm});
            skLineSegment(sketch, "E265.MirrorCS", {"start": v(-487.12, 171.8) * mm, "end": v(-487.12, 176.42) * mm});
            skLineSegment(sketch, "E266.MirrorCS", {"start": v(-469.8, 235.31) * mm, "end": v(-469.8, 239.93) * mm});
            skLineSegment(sketch, "E267.MirrorCS", {"start": v(-469.8, 171.81) * mm, "end": v(-469.8, 176.43) * mm});
            skLineSegment(sketch, "E268", {"start": v(-482.5, 214.52) * mm, "end": v(-482.5, 209.91) * mm});
            skLineSegment(sketch, "E269", {"start": v(-482.5, 209.91) * mm, "end": v(-487.12, 209.9) * mm});
            skLineSegment(sketch, "E270", {"start": v(-349.66, 117.93) * mm, "end": v(-343.58, 117.93) * mm});
            skCircle(sketch, "E271", {"center": v(-343.58, 132.86) * mm, "radius": 1.59 * mm});
            skLineSegment(sketch, "E272", {"start": v(-259.41, 117.93) * mm, "end": v(-264.62, 117.93) * mm});
            skCircle(sketch, "E273", {"center": v(-264.62, 125.68) * mm, "radius": 1.59 * mm});
            skCircle(sketch, "E274", {"center": v(-264.62, 190.68) * mm, "radius": 1.59 * mm});
            skPoint(sketch, "E275.end.orphan", {"position": v(-349.66, 132.86) * mm});
            skPoint(sketch, "E275.start.orphan", {"position": v(-349.66, 125.68) * mm});
            skPoint(sketch, "E276.end.orphan", {"position": v(-259.41, 125.68) * mm});
            skPoint(sketch, "E276.start.orphan", {"position": v(-259.41, 190.68) * mm});
            skSolve(sketch);
        }
        {
            var Q0;
            Q0 = qSketchRegion(id + "F2", true);
            extrude(context, id + "F3", {"entities" : qUnion([Q0]), "depth" : 3.17 * mm});
        }
    });
